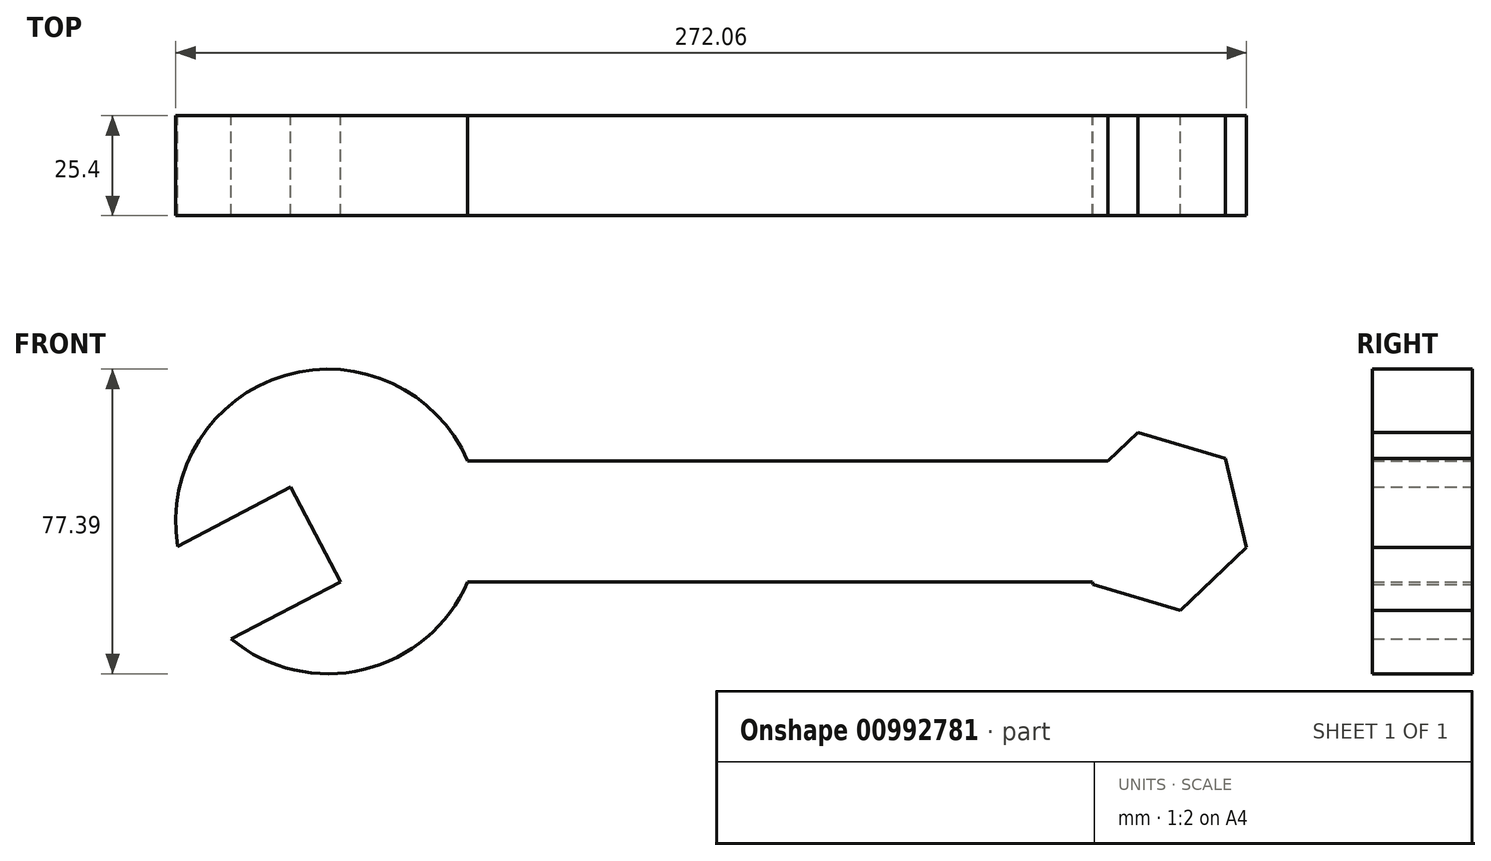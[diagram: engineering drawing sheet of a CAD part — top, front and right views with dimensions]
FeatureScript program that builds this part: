
annotation { "Feature Type Name" : "Feature", "Feature Type Description" : "" }
export const myFeature = defineFeature(function(context is Context, id is Id, definition is map)
    precondition{}
    {
        {
            var Q0;
            Q0=qCreatedBy(makeId("Front.planeOp"),FACE);
            var sketch = newSketch(context, id + "F0", { "sketchPlane" : qUnion([Q0])});
            skLineSegment(sketch, "E0.bottom", {"start": v(-61.15, 60.29) * mm, "end": v(149.97, 60.29) * mm});
            skLineSegment(sketch, "E0.top", {"start": v(-61.15, 29.52) * mm, "end": v(149.97, 29.52) * mm});
            skLineSegment(sketch, "E0.left", {"start": v(-61.15, 60.29) * mm, "end": v(-61.15, 29.52) * mm});
            skLineSegment(sketch, "E0.right", {"start": v(149.97, 60.29) * mm, "end": v(149.97, 29.52) * mm});
            skCircle(sketch, "E1", {"center": v(-61.15, 44.9) * mm, "radius": 38.7 * mm});
            skCircle(sketch, "E2.cCircle", {"center": v(149.97, 44.9) * mm, "radius": 20.09 * mm, "construction": true});
            skLineSegment(sketch, "E2.0", {"start": v(166.8, 60.87) * mm, "end": v(172.21, 38.32) * mm});
            skLineSegment(sketch, "E2.1", {"start": v(172.21, 38.32) * mm, "end": v(155.39, 22.35) * mm});
            skLineSegment(sketch, "E2.2", {"start": v(155.39, 22.35) * mm, "end": v(133.15, 28.94) * mm});
            skLineSegment(sketch, "E2.3", {"start": v(133.15, 28.94) * mm, "end": v(127.73, 51.49) * mm});
            skLineSegment(sketch, "E2.4", {"start": v(127.73, 51.49) * mm, "end": v(144.55, 67.46) * mm});
            skLineSegment(sketch, "E2.5", {"start": v(144.55, 67.46) * mm, "end": v(166.8, 60.87) * mm});
            skPoint(sketch, "E2.0.midPoint", {"position": v(169.5, 49.6) * mm});
            skLineSegment(sketch, "E3", {"start": v(-99.33, 38.6) * mm, "end": v(-70.6, 53.64) * mm});
            skLineSegment(sketch, "E4", {"start": v(-70.6, 53.64) * mm, "end": v(-57.98, 29.52) * mm});
            skLineSegment(sketch, "E5", {"start": v(-57.98, 29.52) * mm, "end": v(-85.71, 15) * mm});
            skSolve(sketch);
        }
        {
            var Q0;
            {var subQ0=sQuery(id+"F0.wireOp",EDGE,"E3");Q0=makeQuery(id+"F0.imprint","IMPRINT",FACE,{"disambiguationData":[TD([[makeQuery(id+"F0.imprint","IMPRINT",EDGE,{"derivedFrom":subQ0}),1.0]])]});}
            var Q1;
            {var subQ0=sQuery(id+"F0.wireOp",EDGE,"E0.right");Q1=makeQuery(id+"F0.imprint","IMPRINT",FACE,{"disambiguationData":[TD([[makeQuery(id+"F0.imprint","IMPRINT",EDGE,{"derivedFrom":subQ0}),1.0]])]});}
            var Q2;
            {var subQ5=sQuery(id+"F0.wireOp",EDGE,"E0.right");Q2=makeQuery(id+"F0.imprint","IMPRINT",FACE,{"disambiguationData":[TD([[makeQuery(id+"F0.imprint","IMPRINT",EDGE,{"derivedFrom":subQ5}),-1.0]])]});}
            var Q3;
            {var subQ5=sQuery(id+"F0.wireOp",EDGE,"E1");var subQ6=sQuery(id+"F0.wireOp",EDGE,"E0.bottom");var subQ7=makeQuery(id+"F0.imprint","INTERSECT",VERTEX,{"derivedFrom":[subQ6,subQ5]});Q3=makeQuery(id+"F0.imprint","IMPRINT",FACE,{"disambiguationData":[TD([[makeQuery(id+"F0.imprint","IMPRINT",EDGE,{"disambiguationData":[TD([[subQ7,-1.0]])],"derivedFrom":subQ6}),-1.0]])]});}
            var Q4;
            {var subQ1=sQuery(id+"F0.wireOp",EDGE,"E0.bottom");var subQ7=sQuery(id+"F0.wireOp",EDGE,"E0.left");var subQ9=makeQuery(id+"F0.imprint","INTERSECT",VERTEX,{"derivedFrom":[subQ1,subQ7]});Q4=makeQuery(id+"F0.imprint","IMPRINT",FACE,{"disambiguationData":[TD([[makeQuery(id+"F0.imprint","IMPRINT",EDGE,{"disambiguationData":[TD([[subQ9,-1.0]])],"derivedFrom":subQ1}),-1.0]])]});}
            var Q5;
            {var subQ0=sQuery(id+"F0.wireOp",EDGE,"E5");Q5=makeQuery(id+"F0.imprint","IMPRINT",FACE,{"disambiguationData":[TD([[makeQuery(id+"F0.imprint","IMPRINT",EDGE,{"derivedFrom":subQ0}),1.0]])]});}
            extrude(context, id + "F1", {"entities" : qUnion([Q0, Q1, Q2, Q3, Q4, Q5]), "depth" : 25.4 * mm, "offsetDistance" : 25.4 * mm});
        }
    });
